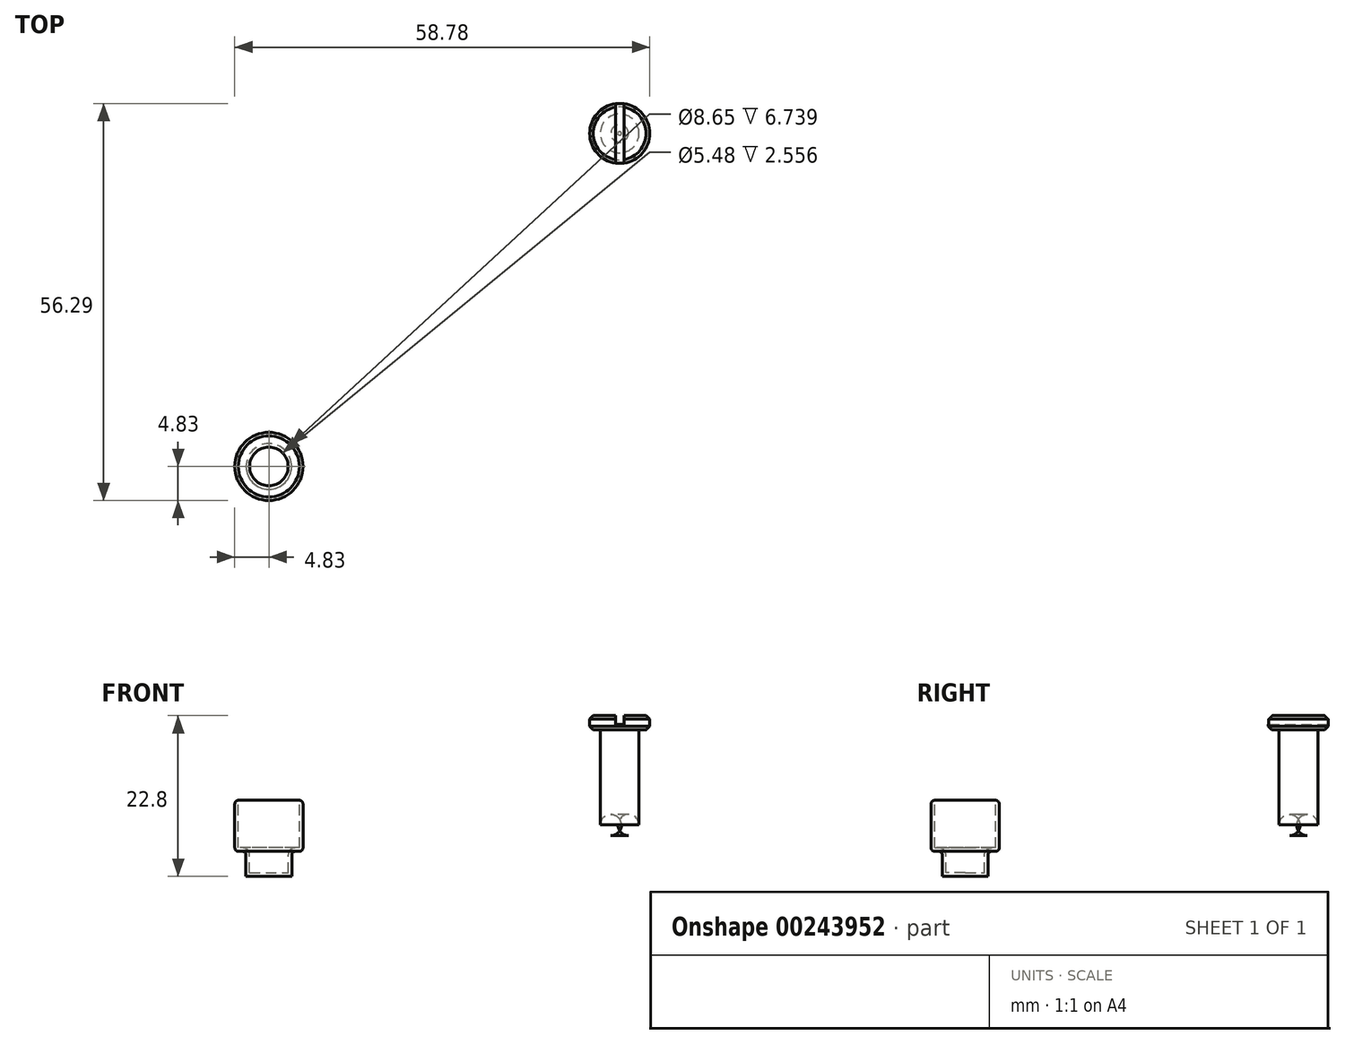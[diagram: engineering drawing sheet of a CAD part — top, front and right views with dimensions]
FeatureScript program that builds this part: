
annotation { "Feature Type Name" : "Feature", "Feature Type Description" : "" }
export const myFeature = defineFeature(function(context is Context, id is Id, definition is map)
    precondition{}
    {
        {
            var Q0;
            Q0=qCreatedBy(makeId("Top.planeOp"),FACE);
            var sketch = newSketch(context, id + "F0", { "sketchPlane" : qUnion([Q0])});
            skCircle(sketch, "E0", {"center": v(0, 0) * mm, "radius": 4.83 * mm});
            skSolve(sketch);
        }
        {
            var Q0;
            Q0 = qSketchRegion(id + "F0", true);
            extrude(context, id + "F1", {"entities" : qUnion([Q0]), "oppositeDirection" : true, "depth" : 7.24 * mm});
        }
        {
            var Q0;
            Q0=makeQuery(id+"F1.opExtrude","CAP_FACE",FACE,{"disambiguationData":[OSD([sQuery(id+"F0.wireOp",EDGE,"E0")])],"isStart":false});
            var sketch = newSketch(context, id + "F2", { "sketchPlane" : qUnion([Q0])});
            skCircle(sketch, "E1", {"center": v(0, 0) * mm, "radius": 3.24 * mm});
            skSolve(sketch);
        }
        {
            var Q0;
            Q0 = qSketchRegion(id + "F2", true);
            extrude(context, id + "F3", {"entities" : qUnion([Q0]), "operationType" : NewBodyOperationType.ADD, "depth" : 3.56 * mm});
        }
        {
            var Q0;
            Q0=makeQuery(id+"F1.opExtrude","CAP_FACE",FACE,{"disambiguationData":[OSD([sQuery(id+"F0.wireOp",EDGE,"E0")])],"isStart":true});
            var Q1;
            Q1=makeQuery(id+"F1.opExtrude","CAP_FACE",FACE,{"disambiguationData":[OSD([sQuery(id+"F0.wireOp",EDGE,"E0")])],"isStart":false});
            fillet(context, id + "F4", {"entities" : qUnion([Q0, Q1]), "radius" : .5 * mm, "tangentPropagation" : true, "allowEdgeOverflow" : false});
        }
        {
            var Q0;
            Q0=makeQuery(id+"F1.opExtrude","CAP_FACE",FACE,{"disambiguationData":[OSD([sQuery(id+"F0.wireOp",EDGE,"E0")])],"isStart":true});
            var Q1;
            Q1=makeQuery(id+"F1.opExtrude","SWEPT_BODY",BODY,{"disambiguationData":[OSD([sQuery(id+"F0.wireOp",EDGE,"E0")])]});
            shell(context, id + "F5", {"isHollow" : true, "entities" : qUnion([Q0]), "parts" : qUnion([Q1]), "thickness" : .5 * mm});
        }
        {
            var Q0;
            Q0=makeQuery(id+"F1.opExtrude","CAP_FACE",FACE,{"disambiguationData":[OSD([sQuery(id+"F0.wireOp",EDGE,"E0")])],"isStart":true});
            extrude(context, id + "F6", {"entities" : qUnion([Q0]), "operationType" : NewBodyOperationType.REMOVE, "oppositeDirection" : true, "depth" : 1 * mm});
        }
        {
            var Q0;
            Q0=qCreatedBy(makeId("Top.planeOp"),FACE);
            var sketch = newSketch(context, id + "F7", { "sketchPlane" : qUnion([Q0])});
            skCircle(sketch, "E2", {"center": v(49.7, 47.21) * mm, "radius": 2.75 * mm});
            skSolve(sketch);
        }
        {
            var Q0;
            Q0 = qSketchRegion(id + "F7", true);
            extrude(context, id + "F8", {"entities" : qUnion([Q0]), "depth" : 10 * mm});
        }
        {
            var Q0;
            Q0=makeQuery(id+"F8.opExtrude","CAP_FACE",FACE,{"disambiguationData":[OSD([sQuery(id+"F7.wireOp",EDGE,"E2")])],"isStart":false});
            var sketch = newSketch(context, id + "F9", { "sketchPlane" : qUnion([Q0])});
            skCircle(sketch, "E3.0", {"center": v(49.7, 47.21) * mm, "radius": 4.25 * mm});
            skSolve(sketch);
        }
        {
            var Q0;
            Q0 = qSketchRegion(id + "F9", true);
            extrude(context, id + "F10", {"entities" : qUnion([Q0]), "operationType" : NewBodyOperationType.ADD, "depth" : 2 * mm});
        }
        {
            var Q0;
            Q0=makeQuery(id+"F10.opExtrude","CAP_FACE",FACE,{"disambiguationData":[OSD([sQuery(id+"F9.wireOp",EDGE,"E3.0")])],"isStart":false});
            var sketch = newSketch(context, id + "F11", { "sketchPlane" : qUnion([Q0])});
            skLineSegment(sketch, "E4.0", {"start": v(49.1, 47.21) * mm, "end": v(49.1, 43) * mm});
            skLineSegment(sketch, "E5.0", {"start": v(50.3, 47.21) * mm, "end": v(50.3, 51.42) * mm});
            skLineSegment(sketch, "E6.0", {"start": v(49.1, 47.21) * mm, "end": v(49.1, 51.42) * mm});
            skLineSegment(sketch, "E7.0", {"start": v(50.3, 47.21) * mm, "end": v(50.3, 43) * mm});
            skArc(sketch, "E8.0", {"start": v(50.3, 51.42) * mm, "mid": v(49.7, 51.46) * mm, "end": v(49.1, 51.42) * mm});
            skArc(sketch, "E9.trimOffspring", {"start": v(49.1, 43) * mm, "mid": v(49.7, 42.96) * mm, "end": v(50.3, 43) * mm});
            skSolve(sketch);
        }
        {
            var Q0;
            Q0 = qSketchRegion(id + "F11", true);
            extrude(context, id + "F12", {"entities" : qUnion([Q0]), "operationType" : NewBodyOperationType.REMOVE, "oppositeDirection" : true, "depth" : 1.25 * mm});
        }
        {
            var Q0;
            {var subQ0=sQuery(id+"F9.wireOp",EDGE,"E3.0");Q0=makeQuery(id+"F12.boolean.opBoolean","SPLIT",EDGE,{"disambiguationData":[TD([makeQuery(id+"F12.opExtrude","SWEPT_FACE",FACE,{"disambiguationData":[OSD([sQuery(id+"F11.wireOp",EDGE,"E4.0"),sQuery(id+"F11.wireOp",EDGE,"E6.0")])]})])],"derivedFrom":makeQuery(id+"F10.opExtrude","CAP_EDGE",EDGE,{"disambiguationData":[OSD([subQ0])],"isStart":false})});}
            var Q1;
            {var subQ0=sQuery(id+"F9.wireOp",EDGE,"E3.0");Q1=makeQuery(id+"F12.boolean.opBoolean","SPLIT",EDGE,{"disambiguationData":[TD([makeQuery(id+"F12.opExtrude","SWEPT_FACE",FACE,{"disambiguationData":[OSD([sQuery(id+"F11.wireOp",EDGE,"E5.0"),sQuery(id+"F11.wireOp",EDGE,"E7.0")])]})])],"derivedFrom":makeQuery(id+"F10.opExtrude","CAP_EDGE",EDGE,{"disambiguationData":[OSD([subQ0])],"isStart":false})});}
            var Q2;
            Q2=makeQuery(id+"F10.opExtrude","CAP_EDGE",EDGE,{"disambiguationData":[OSD([sQuery(id+"F9.wireOp",EDGE,"E3.0")])],"isStart":true});
            chamfer(context, id + "F13", {"entities" : qUnion([Q0, Q1, Q2]), "width" : .5 * mm, "tangentPropagation" : true});
        }
        {
            var Q0;
            Q0=makeQuery(id+"F8.opExtrude","CAP_FACE",FACE,{"disambiguationData":[OSD([sQuery(id+"F7.wireOp",EDGE,"E2")])],"isStart":true});
            extrude(context, id + "F14", {"entities" : qUnion([Q0]), "operationType" : NewBodyOperationType.ADD, "depth" : 5 * mm});
        }
        {
            var Q0;
            Q0=makeQuery(id+"F14.opExtrude","CAP_FACE",FACE,{"disambiguationData":[OSD([sQuery(id+"F7.wireOp",EDGE,"E2")])],"isStart":false});
            fillet(context, id + "F15", {"entities" : qUnion([Q0]), "radius" : 1.5 * mm, "tangentPropagation" : true, "allowEdgeOverflow" : false});
        }
    });
